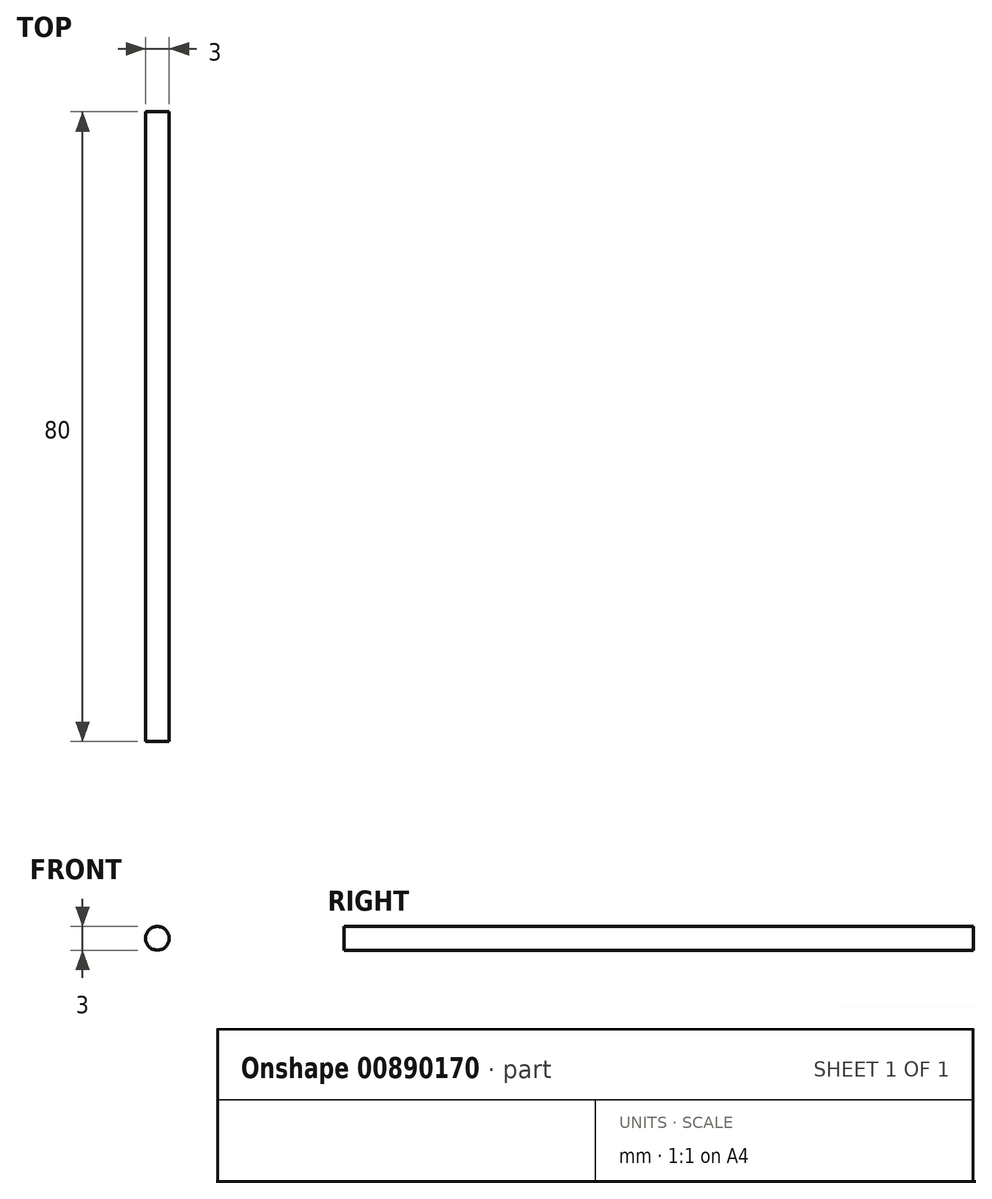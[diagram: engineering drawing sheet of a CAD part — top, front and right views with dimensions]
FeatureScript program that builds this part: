
annotation { "Feature Type Name" : "Feature", "Feature Type Description" : "" }
export const myFeature = defineFeature(function(context is Context, id is Id, definition is map)
    precondition{}
    {
        {
            var Q0;
            Q0=qCreatedBy(makeId("Front.planeOp"),FACE);
            var sketch = newSketch(context, id + "F0", { "sketchPlane" : qUnion([Q0])});
            skCircle(sketch, "E0", {"center": v(0, 0) * mm, "radius": 1.5 * mm});
            skSolve(sketch);
        }
        {
            var Q0;
            Q0=qSketchRegion(id+"F0",true);
            extrude(context, id + "F1", {"entities" : qUnion([Q0]), "depth" : 80 * mm, "offsetDistance" : 25 * mm});
        }
    });
